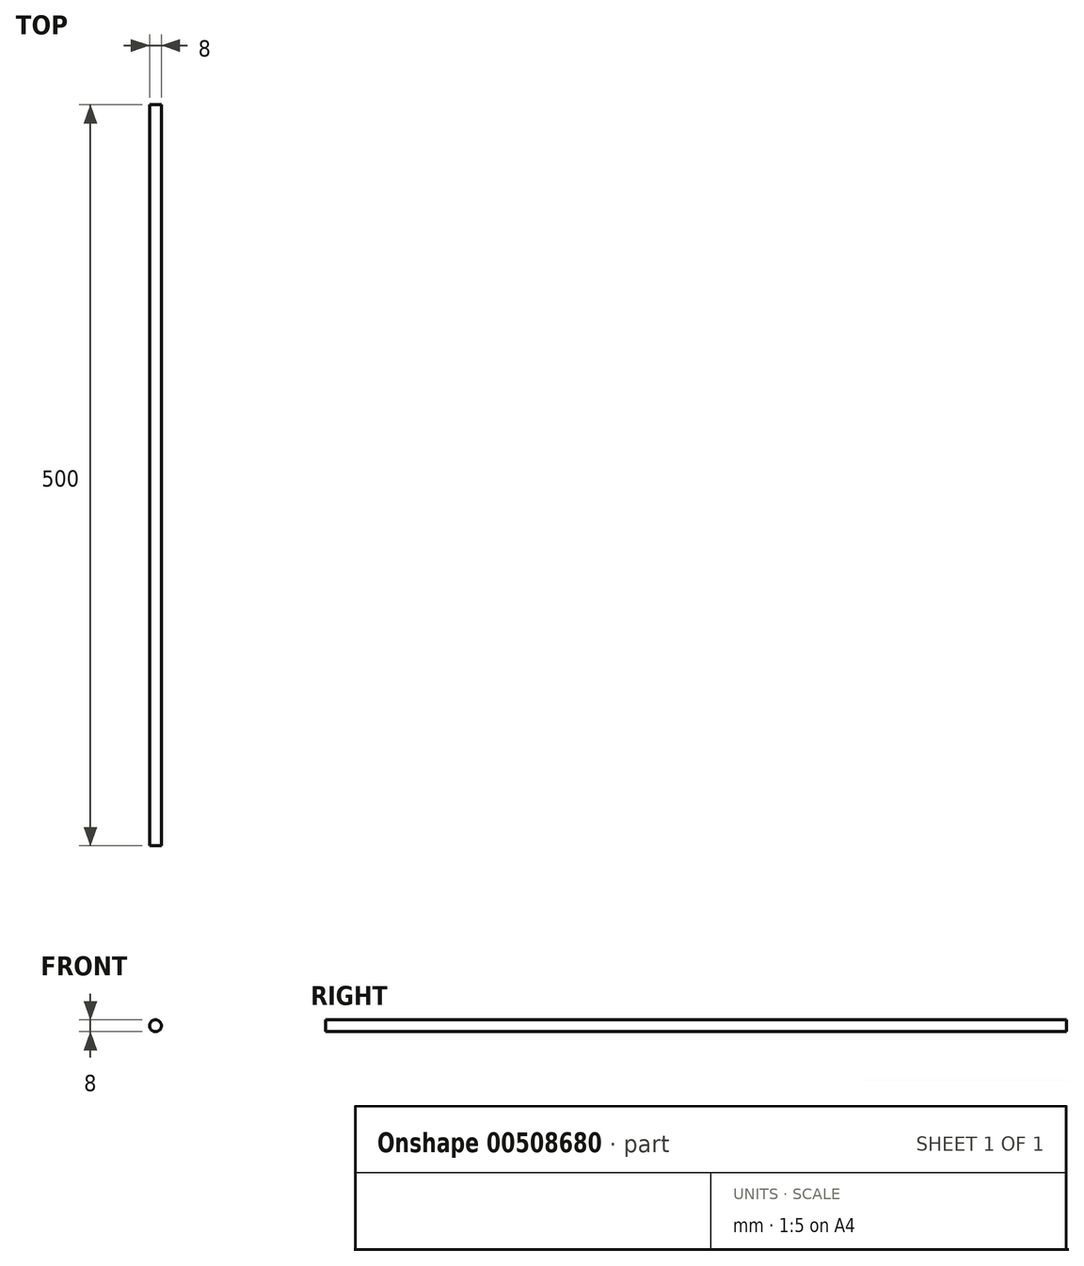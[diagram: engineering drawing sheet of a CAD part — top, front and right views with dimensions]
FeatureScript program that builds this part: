
annotation { "Feature Type Name" : "Feature", "Feature Type Description" : "" }
export const myFeature = defineFeature(function(context is Context, id is Id, definition is map)
    precondition{}
    {
        {
            var Q0;
            Q0=qCreatedBy(makeId("Front.planeOp"),FACE);
            var sketch = newSketch(context, id + "F0", { "sketchPlane" : qUnion([Q0])});
            skCircle(sketch, "E0", {"center": v(0, 0) * mm, "radius": 4 * mm});
            skSolve(sketch);
        }
        {
            var Q0;
            Q0 = qSketchRegion(id + "F0", true);
            extrude(context, id + "F1", {"entities" : qUnion([Q0]), "depth" : 500 * mm, "offsetDistance" : 25 * mm});
        }
    });
